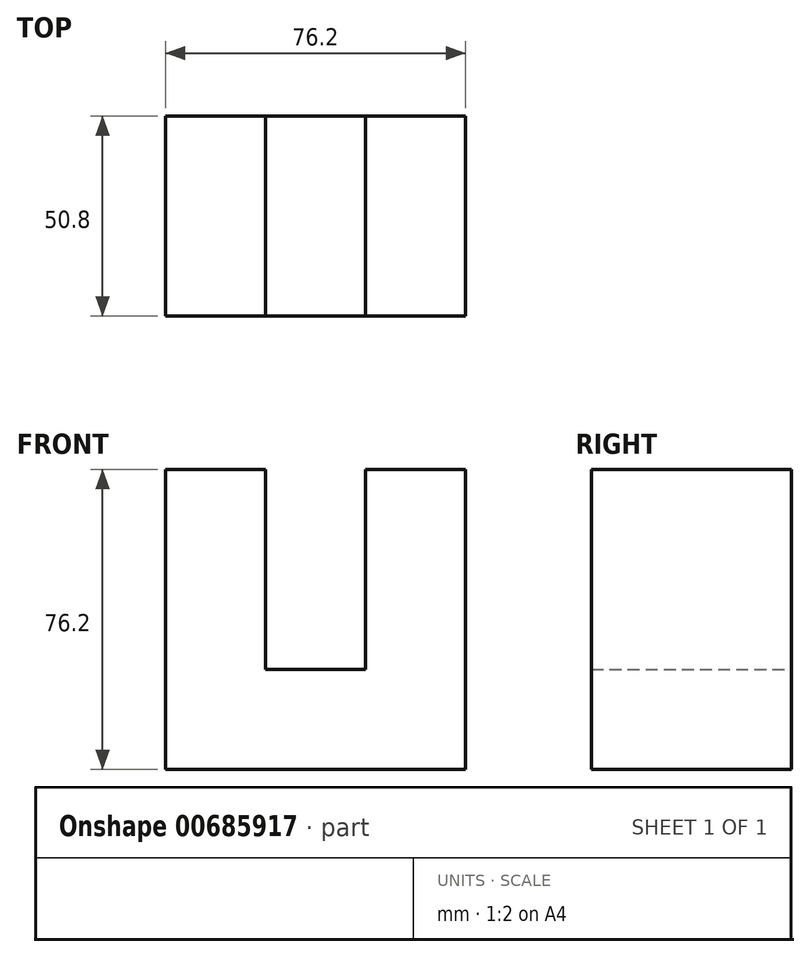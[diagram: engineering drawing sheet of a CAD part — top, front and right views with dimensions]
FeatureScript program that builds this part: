
annotation { "Feature Type Name" : "Feature", "Feature Type Description" : "" }
export const myFeature = defineFeature(function(context is Context, id is Id, definition is map)
    precondition{}
    {
        {
            var Q0;
            Q0=qCreatedBy(makeId("Front.planeOp"),FACE);
            var sketch = newSketch(context, id + "F0", { "sketchPlane" : qUnion([Q0])});
            skLineSegment(sketch, "E0", {"start": v(0, -40.58) * mm, "end": v(-76.2, -40.58) * mm});
            skLineSegment(sketch, "E1", {"start": v(-76.2, -40.58) * mm, "end": v(-76.2, 35.62) * mm});
            skLineSegment(sketch, "E2", {"start": v(-76.2, 35.62) * mm, "end": v(-50.8, 35.62) * mm});
            skLineSegment(sketch, "E3", {"start": v(-50.8, 35.62) * mm, "end": v(-50.8, -15.18) * mm});
            skLineSegment(sketch, "E4", {"start": v(-50.8, -15.18) * mm, "end": v(-25.4, -15.18) * mm});
            skLineSegment(sketch, "E5", {"start": v(-25.4, -15.18) * mm, "end": v(-25.4, 35.62) * mm});
            skLineSegment(sketch, "E6", {"start": v(-25.4, 35.62) * mm, "end": v(0, 35.62) * mm});
            skLineSegment(sketch, "E7", {"start": v(0, 35.62) * mm, "end": v(0, -40.58) * mm});
            skSolve(sketch);
        }
        {
            var Q0;
            Q0 = qSketchRegion(id + "F0", true);
            extrude(context, id + "F1", {"entities" : qUnion([Q0]), "depth" : 50.8 * mm, "offsetDistance" : 25.4 * mm});
        }
    });
